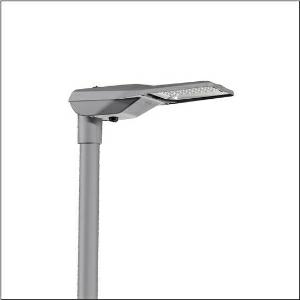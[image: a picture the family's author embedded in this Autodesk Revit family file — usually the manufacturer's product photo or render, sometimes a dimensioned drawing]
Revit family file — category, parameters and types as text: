
# Revit family: streetlight_sl_21_iq_mini___pl52_5xe2h31y08hb_fa04
name_source: partatom
category: Lighting Fixtures
units: mm (PartAtom-declared; Revit-internal decimal feet)

## family parameters
Cut with Voids When Loaded = No
Host = Face
Light Source = No
Part Type = Normal
Room Calculation Point = No
Round Connector Dimension = Use Diameter
Shared = No

## types (1)
- --- (1 x LED, 9580 lm, 71 W, 3000K)
    Apparent Load = 71 VA
    CIE Flux Codes = 27 59 98 100 100
    Color Rendering = 70
    Color Temperature = 3000K
    Default Elevation = 1800 mm
    Description = Streetlight SL 21 iQ mini, mast luminaire, primary light control with lens, of PMMA, primary optical cover: cover, of toughened safety glass, transparent, light distribution: PL52, light emission: direct distribution, primary light characteristic: asymmetric, installation type: post-top, side-entry, LED, High Power LED, rated luminous flux: 9.580lm, luminous efficacy: 135lm/W, light colour: 730, colour temperature: 3000K, control gear: iQ-Street Remote, D4i with power reduction, control: pre-setting: logarithmic dimming characteristic, Street-Remote, Auto-Match, Temp-Guard, Lumen-Switch, Night-Set, Smart-Wire, Light-Fading, Desk-Remote (wireless, voltage-free reading and setting of iQ features in the workshop via application-optimized NFC function/RFID function), optimised constant luminous flux control (CLO 2.0), mains connection: 220..240V, AC, 50/60Hz, start of lifetime: 71W, end of service life: 75W, reduction: 30W, luminaire housing, of diecast aluminium, powder-coated, SITECO metallic grey (DB 702S), corrosivity category C5 high according to DIN EN ISO 12944, please order mast flange separately, inclination adjustable: 0°, 5°, 10°, 15°, sealing non-destructively replaceable, multi-level sealing system, length: 628mm, width: 235mm, height: 110mm, mast flange for spigot size: 42mm (side-entry): 5XC10008XM4, 60/48mm (side-entry/post-top): 5XC10108XM2, 76/60mm (side-entry/post-top): 5XC10108XM1, mounting height: 4..8m, Smart Interface below and above, protection rating (complete): IP66, insulation class (complete): insulation class II (safety insulation), certification: CE, ENEC, ENEC+, VDE, impact resistance: IK10, permissible operating ambient temperature for outdoor applications: -40..+50°C, standard-compliant lighting for roads and squares, packaging unit: 1 piece

Light Distribution: PL52
    Height = 110 mm
    Lamp = 1 x LED
    Lamp Light Flux = 9580 lm
    Lamp Power = 71 W
    Lamp count = 1
    Length = 625 mm
    Luminous efficacy = 135 lm/W
    Manufacturer = Siteco
    ModVariant = No
    Model = 5XE2H31Y08HB
    Number of Poles = 1
    OnlyDefault = Yes
    Power Factor = 1
    Product Name = Streetlight SL 21 iQ mini | PL52
    Product group = mast luminaire | pylon top
    ProductGroupID = 6100
    Protection Class = Protection class II
    Protection Degree = IP 66
    RLX_Detail_Level = 1
    RLX_Emergency_Light_Flux = 0 lm
    RLX_Emergency_Type = 0
    RLX_Emergency_Type_DB = No
    RlxData = <blob elided: 102373 chars, md5=4b8843fd>
    Socket = socket
    Standby Power = 0 W
    System Light Flux = 9580 lm
    System Power = 71 W
    Type Comments = factory setting: luminous flux: 100 % | dim-lin: 254 | 716 mA
    Type Image = l_1003514.jpg
    URL = http://relux.com
    VarID = @adj_116035
    Voltage = 0 V
    Weight = 0.00 kg
    Width = 234 mm

## geometry (parser evidence)
native form markers: Blend x4, Sweep x9
no freeform markers — native parametric forms only
